# Revit family: Sink-Drop_In-KOHLER-Cimarron-K-2351
name_source: partatom
category: Plumbing Fixtures
units: mm (PartAtom-declared; Revit-internal decimal feet)

## family parameters
Cut with Voids When Loaded = No
Host = Face
OmniClass Number = 23.45.05.14.14
OmniClass Title = Sinks/Lavatories
Part Type = Normal
Room Calculation Point = No
Round Connector Dimension = Use Diameter
Shared = No

## types (1)
- Not a Type-See Type Catalog
    ADA Compliant = Yes
    Assembly Code = D2010400
    Date Modified = September 8, 2017
    Default Elevation = 36"
    Drain Included = No
    Edition number = 1
    Faucet Hole Spacing = 4"
    Finish = Default
    Flow Rate = 0 GPM
    Height = 7 7/8"
    Length = 23"
    Manufacturer = KOHLER Co.
    MasterFormat 1995 = 15410
    MasterFormat 2004 = 22.41.16
    Material = Vitreous China
    Model = 0
    Pressure = 0.00 psi
    Product Documentation Link = http://www.us.kohler.com
    Product Guid = 92d633e2-f189-4225-a24d-62e98f444a14
    Product Name = Cimarron
    Product Page URL = http://www.us.kohler.com
    Product data url = https://bimobject.com
    Type = 0
    URL = http://www.us.kohler.com
    Waste Connection = Yes
    Waste Water Outlet = Waste Water Outlet
    Width = 18 3/16"

## geometry (parser evidence)
native form markers: Sweep x4
no freeform markers — native parametric forms only
